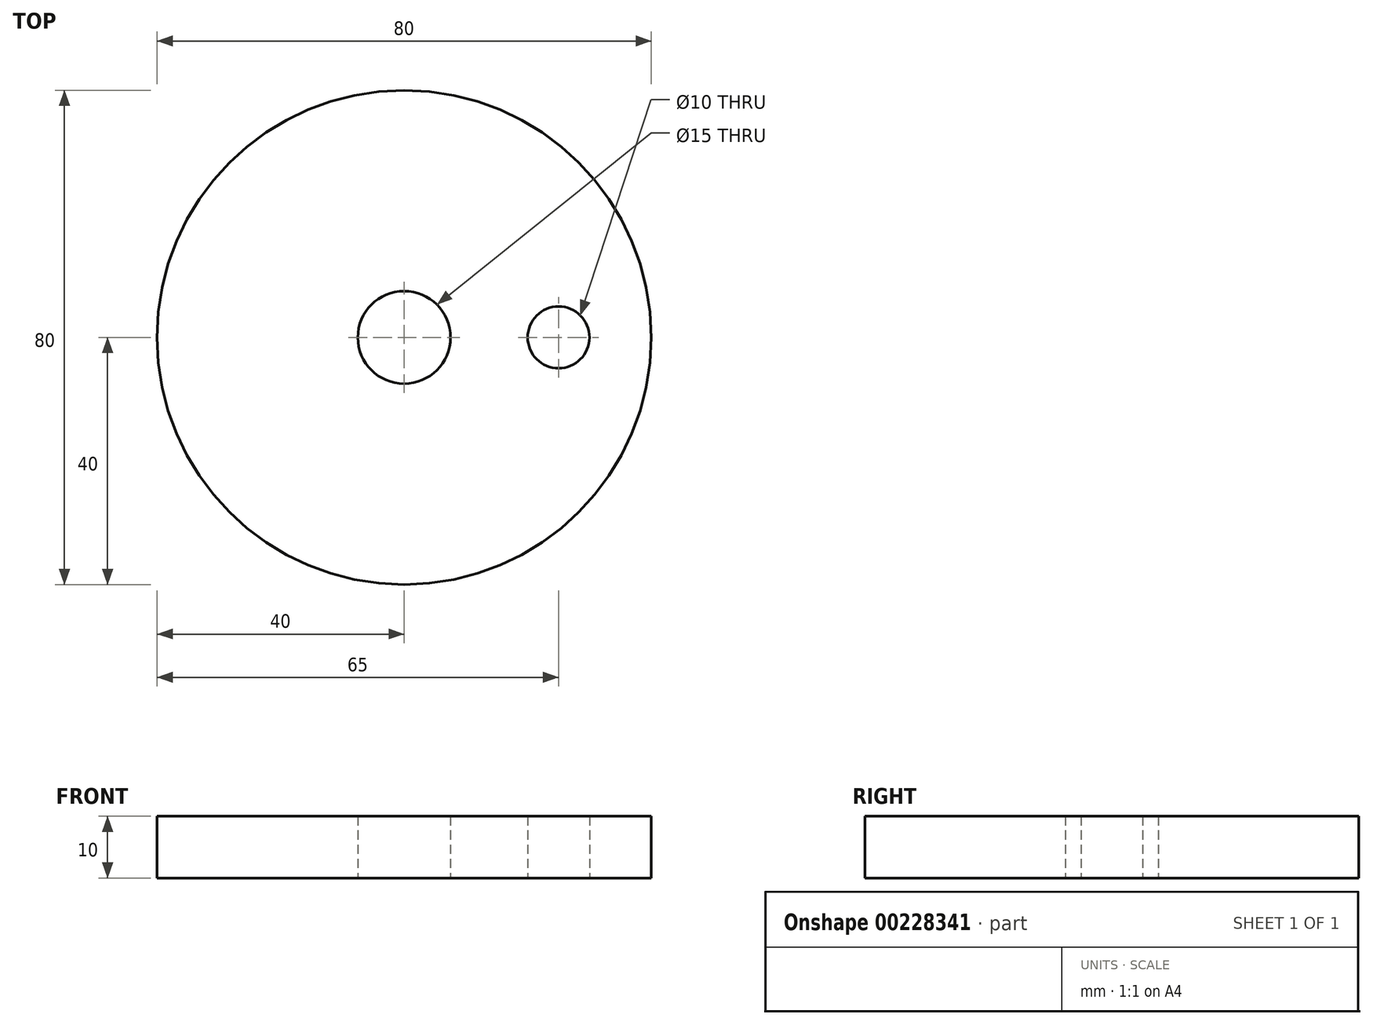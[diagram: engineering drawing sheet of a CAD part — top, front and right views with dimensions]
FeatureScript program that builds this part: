
annotation { "Feature Type Name" : "Feature", "Feature Type Description" : "" }
export const myFeature = defineFeature(function(context is Context, id is Id, definition is map)
    precondition{}
    {
        {
            var Q0;
            Q0=qCreatedBy(makeId("Top.planeOp"),FACE);
            var sketch = newSketch(context, id + "F0", { "sketchPlane" : qUnion([Q0])});
            skCircle(sketch, "E0", {"center": v(0, 0) * mm, "radius": 40 * mm});
            skSolve(sketch);
        }
        {
            var Q0;
            Q0=makeQuery(id+"F0.imprint","IMPRINT",FACE,{"disambiguationData":[TD([[makeQuery(id+"F0.imprint","IMPRINT",EDGE,{"derivedFrom":sQuery(id+"F0.wireOp",EDGE,"E0")}),1.0]])]});
            extrude(context, id + "F1", {"entities" : qUnion([Q0]), "depth" : 10 * mm});
        }
        {
            var Q0;
            Q0=makeQuery(id+"F1.opExtrude","CAP_FACE",FACE,{"disambiguationData":[OSD([sQuery(id+"F0.wireOp",EDGE,"E0")])],"isStart":false});
            var sketch = newSketch(context, id + "F2", { "sketchPlane" : qUnion([Q0])});
            skPoint(sketch, "E1", {"position": v(25, 0) * mm});
            skSolve(sketch);
        }
        {
            var Q0;
            Q0=sQuery(id+"F2.wireOp",VERTEX,"E1");
            var Q1;
            Q1=makeQuery(id+"F1.opExtrude","SWEPT_BODY",BODY,{"disambiguationData":[OSD([sQuery(id+"F0.wireOp",EDGE,"E0")])]});
            hole(context, id + "F4", {"style" : HoleStyle.SIMPLE, "endStyle" : HoleEndStyle.THROUGH, "holeDiameter" : 10 * mm, "locations" : qUnion([Q0]), "scope" : qUnion([Q1]), "isTappedThrough" : true, "startStyle" : HoleStartStyle.PART});
        }
        {
            var Q0;
            Q0=makeQuery(id+"F1.opExtrude","CAP_FACE",FACE,{"disambiguationData":[OSD([sQuery(id+"F0.wireOp",EDGE,"E0")])],"isStart":false});
            var sketch = newSketch(context, id + "F3", { "sketchPlane" : qUnion([Q0])});
            skPoint(sketch, "E2", {"position": v(0, 0) * mm});
            skSolve(sketch);
        }
        {
            var Q0;
            Q0=sQuery(id+"F3.wireOp",VERTEX,"E2");
            var Q1;
            Q1=makeQuery(id+"F1.opExtrude","SWEPT_BODY",BODY,{"disambiguationData":[OSD([sQuery(id+"F0.wireOp",EDGE,"E0")])]});
            hole(context, id + "F5", {"style" : HoleStyle.SIMPLE, "endStyle" : HoleEndStyle.THROUGH, "holeDiameter" : 15 * mm, "locations" : qUnion([Q0]), "scope" : qUnion([Q1]), "isTappedThrough" : true, "startStyle" : HoleStartStyle.PART});
        }
    });
